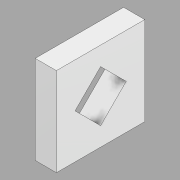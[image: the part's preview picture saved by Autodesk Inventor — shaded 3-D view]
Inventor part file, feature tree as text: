
AUTODESK INVENTOR PART (.ipt)
format: ipt  version: 2020 (Build 240168000, 168)  size: 99,328 bytes
history: native  units: in
note: dims shown in document units (in); Inventor stores cm internally (conversion verified against a paired STEP export)
features: extrude x1, sketch x1
ambient origin geometry x8: Origin, YZ Plane, XZ Plane, XY Plane, X Axis, Y Axis, Z Axis, Center Point
bodies: Solid1 (feature_tree)
feature tree (2):
  extrude  "Extrusion1"  Depth=2.5in
  sketch  "Sketch1"  dims[d0=1.0in d1=1.0in d3=0.2in d4=0.2in d7=2.5in d8=2.5in d9=0.6in d10=0.0in]
